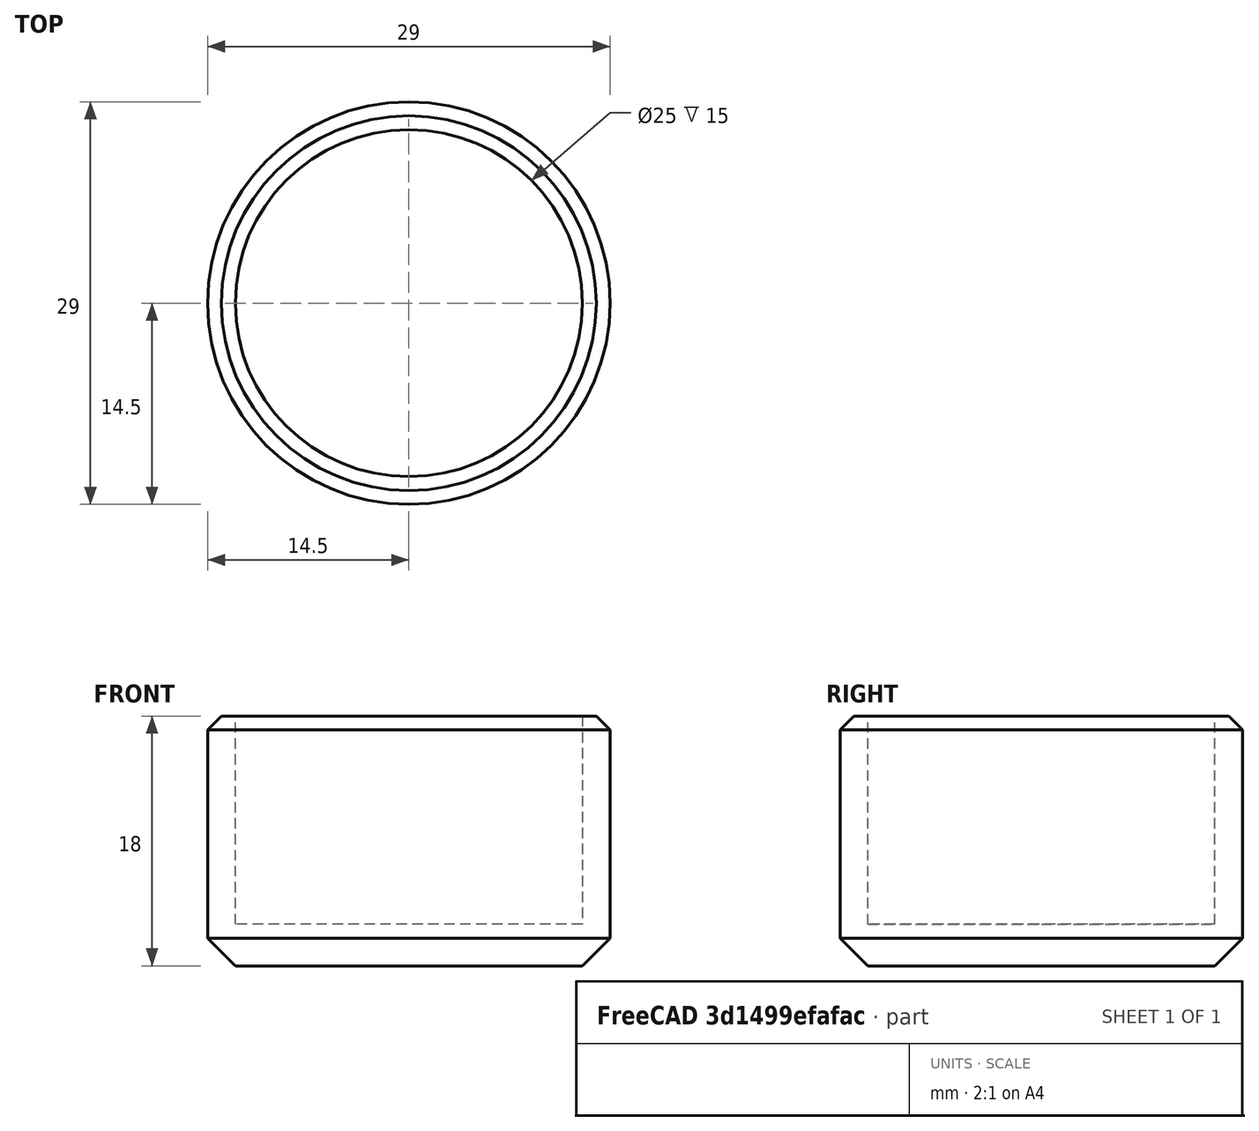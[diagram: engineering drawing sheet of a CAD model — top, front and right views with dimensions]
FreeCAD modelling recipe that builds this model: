
FCSTD DOCUMENT  (FreeCAD 0.21R33771 (Git))
Label: J-Pole_433_Cap
Comment: J-Pole antenna tube cap (flexible material)
License: CC BY-SA 4.0 (SPDX-ID: CC-BY-SA-4.0)
LicenseURL: https://creativecommons.org/licenses/by-sa/4.0/legalcode.txt
objects: Sketcher::SketchObject×2, PartDesign::Chamfer×2, PartDesign::Pad×1, PartDesign::Pocket×1, PartDesign::Body×1, Mesh::Feature×1
note: 11 computed .brp shape members not serialized (recipe doc carries the construction recipe); baked Part::Feature solids carry a one-line shape summary decoded from their .brp

FEATURE [Sketcher::SketchObject] Sketch
  FullyConstrained = true
  MapMode = 5
  Support = -> [XY_Plane]
  sketch-geometry (1):
    g0: Circle CenterX=0 CenterY=0 CenterZ=0 NormalX=0 NormalY=0 NormalZ=1 AngleXU=0 Radius=14.5
  constraints (2):
    c: Coincident(g0,g-1)
    c: Radius(g0) = 14.5
FEATURE [PartDesign::Pad] Pad
  Direction = (0,0,1)
  Length = 18
  Length2 = 10
  Profile = -> Sketch
  ReferenceAxis = -> Sketch [N_Axis]
  Type = 0
FEATURE [Sketcher::SketchObject] Sketch001
  FullyConstrained = true
  MapMode = 5
  Placement = pos=(0,0,18) rot=(0,0,1;0rad)
  Support = -> [Pad]
  sketch-geometry (1):
    g0: Circle CenterX=0 CenterY=0 CenterZ=0 NormalX=0 NormalY=0 NormalZ=1 AngleXU=0 Radius=12.5
  constraints (2):
    c: Coincident(g0,g-1)
    c: Radius(g0) = 12.5
FEATURE [PartDesign::Pocket] Pocket
  BaseFeature = -> Pad
  Direction = (0,0,-1)
  Length = 15
  Length2 = 5
  Profile = -> Sketch001
  ReferenceAxis = -> Sketch001 [N_Axis]
  Type = 0
FEATURE [PartDesign::Chamfer] Chamfer
  Angle = 45
  Base = -> Pocket [Edge2]
  BaseFeature = -> Pocket
  ChamferType = 0
  FlipDirection = false
  Size = 2
  Size2 = 1
  SupportTransform = false
  UseAllEdges = false
FEATURE [PartDesign::Chamfer] Chamfer001
  Angle = 45
  Base = -> Chamfer [Edge3]
  BaseFeature = -> Chamfer
  ChamferType = 0
  FlipDirection = false
  Size = 1
  Size2 = 1
  SupportTransform = false
  UseAllEdges = false
FEATURE [PartDesign::Body] Body
  Group = -> [Sketch,Pad,Sketch001,Pocket,Chamfer,Chamfer001]
  Origin = -> Origin
  Tip = -> Chamfer001
FEATURE [Mesh::Feature] Mesh  label="J-Pole_433_Cap"
